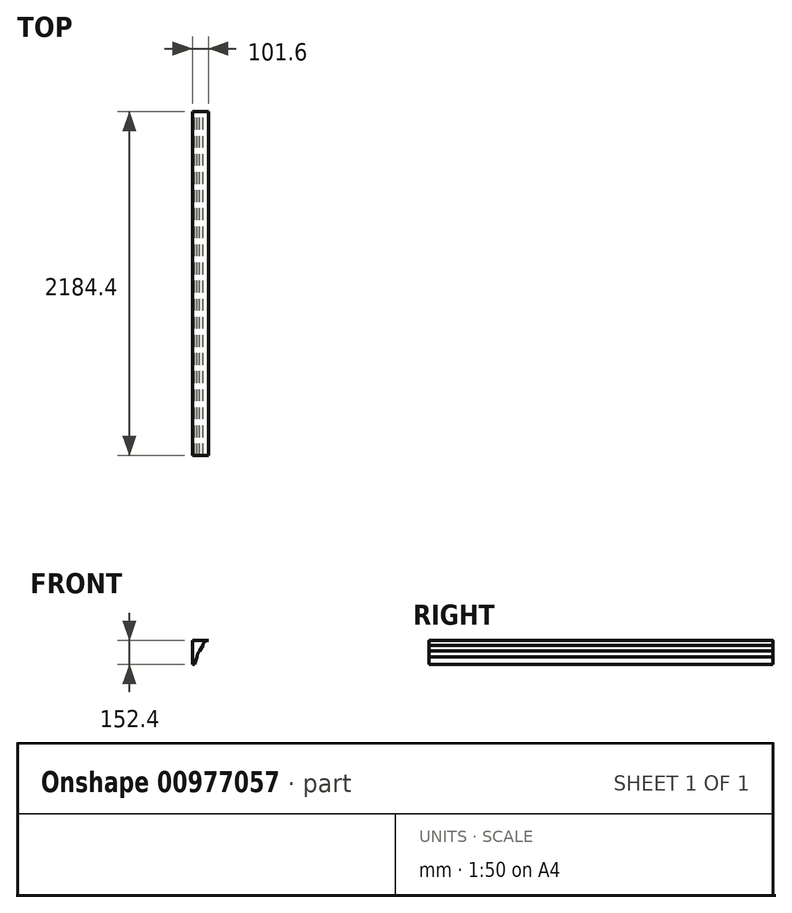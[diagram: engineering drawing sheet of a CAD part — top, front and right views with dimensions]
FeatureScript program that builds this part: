
annotation { "Feature Type Name" : "Feature", "Feature Type Description" : "" }
export const myFeature = defineFeature(function(context is Context, id is Id, definition is map)
    precondition{}
    {
        {
            var Q0;
            Q0=qCreatedBy(makeId("Front.planeOp"),FACE);
            var sketch = newSketch(context, id + "F0", { "sketchPlane" : qUnion([Q0])});
            skLineSegment(sketch, "E0", {"start": v(0, 0) * mm, "end": v(0, 152.4) * mm});
            skLineSegment(sketch, "E1", {"start": v(0, 152.4) * mm, "end": v(101.6, 152.4) * mm});
            skArc(sketch, "E2", {"start": v(101.6, 152.4) * mm, "mid": v(78.15, 143.28) * mm, "end": v(67.01, 120.72) * mm});
            skLineSegment(sketch, "E3", {"start": v(67.01, 120.72) * mm, "end": v(46.98, 84.82) * mm});
            skArc(sketch, "E4", {"start": v(46.98, 84.82) * mm, "mid": v(34.64, 67.81) * mm, "end": v(30.9, 47.13) * mm});
            skLineSegment(sketch, "E5", {"start": v(0, 0) * mm, "end": v(14.72, 0) * mm});
            skLineSegment(sketch, "E6", {"start": v(14.72, 0) * mm, "end": v(30.9, 47.13) * mm});
            skSolve(sketch);
        }
        {
            var Q0;
            Q0 = qSketchRegion(id + "F0", true);
            extrude(context, id + "F1", {"entities" : qUnion([Q0]), "endBound" : BoundingType.SYMMETRIC, "depth" : 2184.4 * mm, "offsetDistance" : 25.4 * mm});
        }
    });
